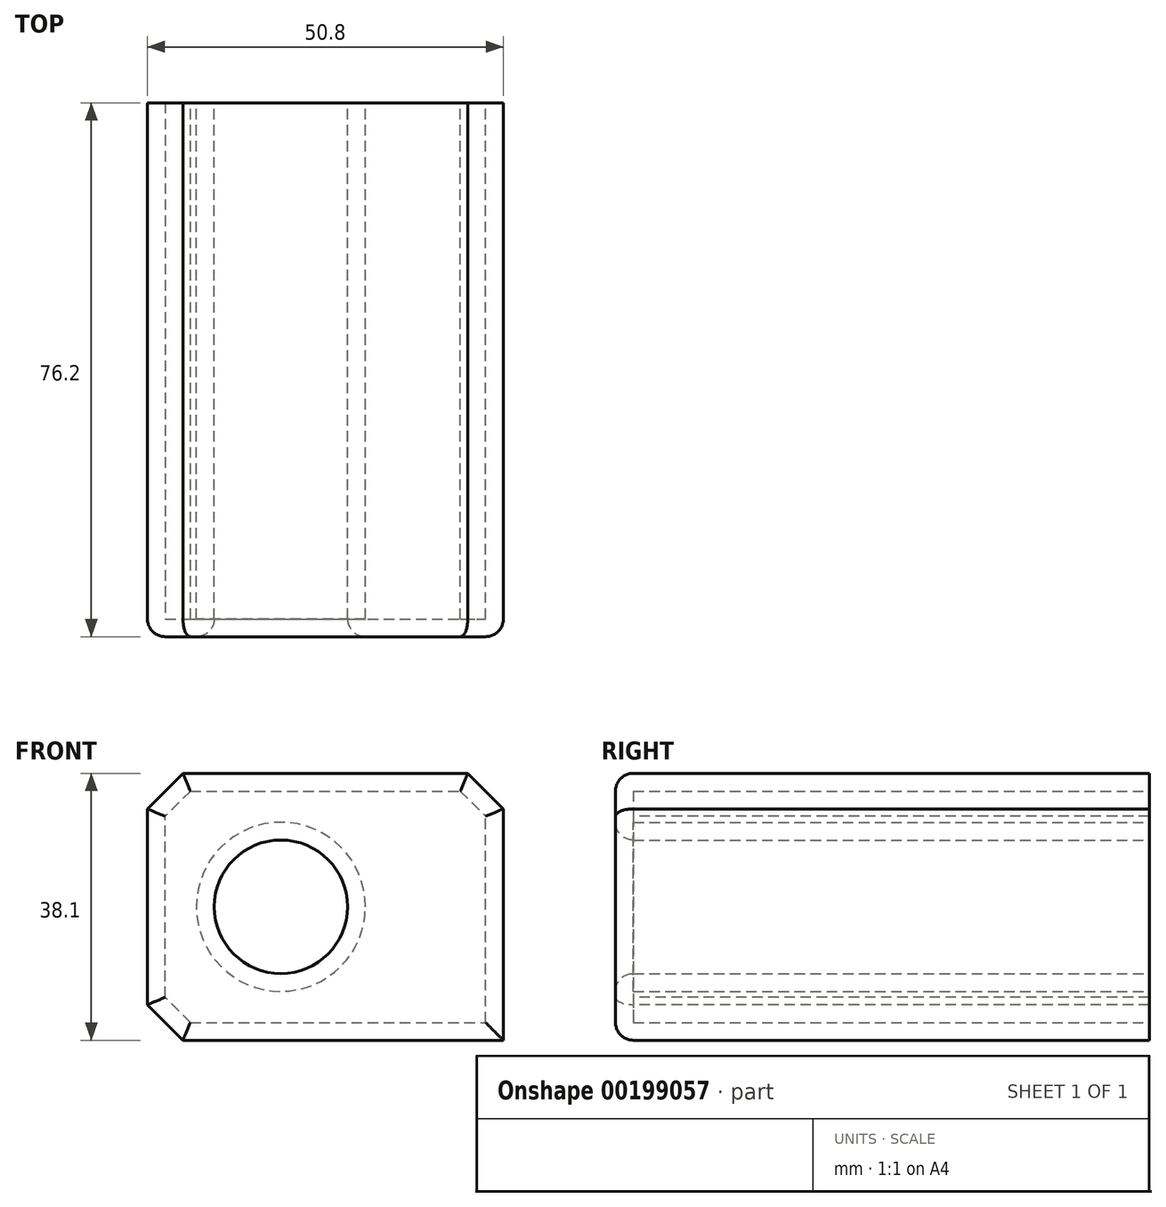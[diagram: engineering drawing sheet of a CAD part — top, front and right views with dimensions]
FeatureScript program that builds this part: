
annotation { "Feature Type Name" : "Feature", "Feature Type Description" : "" }
export const myFeature = defineFeature(function(context is Context, id is Id, definition is map)
    precondition{}
    {
        {
            var Q0;
            Q0=qCreatedBy(makeId("Front.planeOp"),FACE);
            var sketch = newSketch(context, id + "F0", { "sketchPlane" : qUnion([Q0])});
            skLineSegment(sketch, "E0.bottom", {"start": v(0, 0) * mm, "end": v(50.8, 0) * mm});
            skLineSegment(sketch, "E0.top", {"start": v(0, 38.1) * mm, "end": v(50.8, 38.1) * mm});
            skLineSegment(sketch, "E0.left", {"start": v(0, 0) * mm, "end": v(0, 38.1) * mm});
            skLineSegment(sketch, "E0.right", {"start": v(50.8, 0) * mm, "end": v(50.8, 38.1) * mm});
            skCircle(sketch, "E1", {"center": v(19.05, 19.05) * mm, "radius": 9.53 * mm});
            skPoint(sketch, "E1.centerSnap0", {"position": v(0, 19.05) * mm});
            skSolve(sketch);
        }
        {
            var Q0;
            Q0=makeQuery(id+"F0.imprint","IMPRINT",FACE,{"disambiguationData":[TD([[makeQuery(id+"F0.imprint","IMPRINT",EDGE,{"derivedFrom":sQuery(id+"F0.wireOp",EDGE,"E0.bottom")}),1.0]])]});
            extrude(context, id + "F1", {"entities" : qUnion([Q0]), "depth" : 76.2 * mm});
        }
        {
            var Q0;
            Q0=makeQuery(id+"F1.opExtrude","SWEPT_EDGE",EDGE,{"disambiguationData":[OSD([sQuery(id+"F0.wireOp",EDGE,"E0.bottom"),sQuery(id+"F0.wireOp",EDGE,"E0.left")])]});
            chamfer(context, id + "F2", {"entities" : qUnion([Q0]), "width" : 5.08 * mm, "tangentPropagation" : true});
        }
        {
            var Q0;
            Q0=makeQuery(id+"F1.opExtrude","SWEPT_EDGE",EDGE,{"disambiguationData":[OSD([sQuery(id+"F0.wireOp",EDGE,"E0.top"),sQuery(id+"F0.wireOp",EDGE,"E0.left")])]});
            var Q1;
            Q1=makeQuery(id+"F1.opExtrude","SWEPT_EDGE",EDGE,{"disambiguationData":[OSD([sQuery(id+"F0.wireOp",EDGE,"E0.top"),sQuery(id+"F0.wireOp",EDGE,"E0.right")])]});
            chamfer(context, id + "F3", {"entities" : qUnion([Q0, Q1]), "width" : 5.08 * mm, "tangentPropagation" : true});
        }
        {
            var Q0;
            Q0=makeQuery(id+"F1.opExtrude","CAP_FACE",FACE,{"disambiguationData":[OSD([sQuery(id+"F0.wireOp",EDGE,"E0.bottom"),sQuery(id+"F0.wireOp",EDGE,"E0.top"),sQuery(id+"F0.wireOp",EDGE,"E0.left"),sQuery(id+"F0.wireOp",EDGE,"E0.right"),sQuery(id+"F0.wireOp",EDGE,"E1")])],"isStart":false});
            fillet(context, id + "F4", {"entities" : qUnion([Q0]), "radius" : 2.54 * mm, "tangentPropagation" : true, "allowEdgeOverflow" : false});
        }
        {
            var Q0;
            Q0=makeQuery(id+"F1.opExtrude","CAP_FACE",FACE,{"disambiguationData":[OSD([sQuery(id+"F0.wireOp",EDGE,"E0.bottom"),sQuery(id+"F0.wireOp",EDGE,"E0.top"),sQuery(id+"F0.wireOp",EDGE,"E0.left"),sQuery(id+"F0.wireOp",EDGE,"E0.right"),sQuery(id+"F0.wireOp",EDGE,"E1")])],"isStart":true});
            shell(context, id + "F5", {"entities" : qUnion([Q0]), "thickness" : 2.54 * mm});
        }
    });
